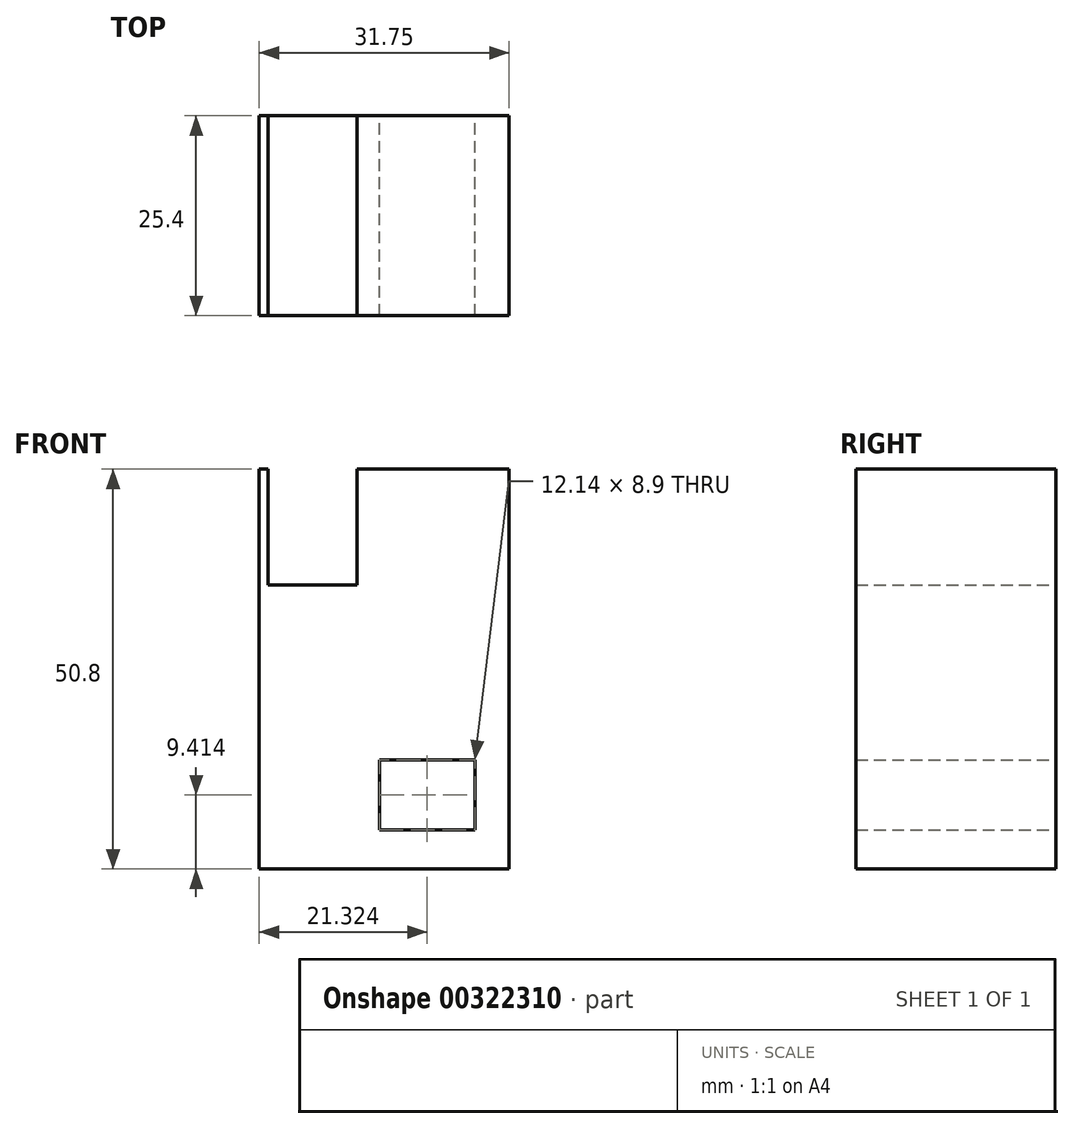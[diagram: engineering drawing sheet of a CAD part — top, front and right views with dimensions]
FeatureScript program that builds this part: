
annotation { "Feature Type Name" : "Feature", "Feature Type Description" : "" }
export const myFeature = defineFeature(function(context is Context, id is Id, definition is map)
    precondition{}
    {
        {
            var Q0;
            Q0=qCreatedBy(makeId("Front.planeOp"),FACE);
            var sketch = newSketch(context, id + "F0", { "sketchPlane" : qUnion([Q0])});
            skLineSegment(sketch, "E0.bottom", {"start": v(25.4, -25.4) * mm, "end": v(-25.4, -25.4) * mm});
            skLineSegment(sketch, "E0.top", {"start": v(25.4, 25.4) * mm, "end": v(-25.4, 25.4) * mm});
            skLineSegment(sketch, "E0.left", {"start": v(25.4, -25.4) * mm, "end": v(25.4, 25.4) * mm});
            skLineSegment(sketch, "E0.right", {"start": v(-25.4, -25.4) * mm, "end": v(-25.4, 25.4) * mm});
            skPoint(sketch, "E0.middle", {"position": v(0, 0) * mm});
            skLineSegment(sketch, "E1", {"start": v(-25.4, -25.4) * mm, "end": v(0, -69.4) * mm});
            skLineSegment(sketch, "E2", {"start": v(25.4, -25.4) * mm, "end": v(0, -69.4) * mm});
            skLineSegment(sketch, "E3", {"start": v(-5.26, 25.4) * mm, "end": v(-5.26, 10.72) * mm});
            skLineSegment(sketch, "E4", {"start": v(6.07, 25.4) * mm, "end": v(6.07, 10.72) * mm});
            skLineSegment(sketch, "E5", {"start": v(-5.26, 10.72) * mm, "end": v(6.07, 10.72) * mm});
            skLineSegment(sketch, "E6", {"start": v(-20.24, -11.53) * mm, "end": v(-10.52, -11.53) * mm});
            skLineSegment(sketch, "E7", {"start": v(-20.24, -11.53) * mm, "end": v(-20.24, -20.84) * mm});
            skLineSegment(sketch, "E8", {"start": v(-10.52, -11.53) * mm, "end": v(-10.52, -21.25) * mm});
            skLineSegment(sketch, "E9", {"start": v(-10.52, -21.25) * mm, "end": v(-20.24, -20.84) * mm});
            skLineSegment(sketch, "E10", {"start": v(8.9, -11.53) * mm, "end": v(21.04, -11.53) * mm});
            skLineSegment(sketch, "E11", {"start": v(8.9, -11.53) * mm, "end": v(8.9, -20.44) * mm});
            skLineSegment(sketch, "E12", {"start": v(8.9, -20.44) * mm, "end": v(21.04, -20.44) * mm});
            skLineSegment(sketch, "E13", {"start": v(21.04, -20.44) * mm, "end": v(21.04, -11.53) * mm});
            skLineSegment(sketch, "E14", {"start": v(-15.38, -11.53) * mm, "end": v(-15.38, -21.04) * mm});
            skLineSegment(sketch, "E15", {"start": v(-20.24, -16.19) * mm, "end": v(-10.52, -16.6) * mm});
            skLineSegment(sketch, "E16", {"start": v(14.97, -11.53) * mm, "end": v(14.97, -21.04) * mm});
            skLineSegment(sketch, "E17", {"start": v(21.04, -15.99) * mm, "end": v(8.9, -15.99) * mm});
            skLineSegment(sketch, "E18.0", {"start": v(-6.35, -25.4) * mm, "end": v(-6.35, 25.4) * mm});
            skSolve(sketch);
        }
        {
            var Q0;
            {var subQ5=sQuery(id+"F0.wireOp",EDGE,"E0.left");Q0=makeQuery(id+"F0.imprint","IMPRINT",FACE,{"disambiguationData":[TD([[makeQuery(id+"F0.imprint","IMPRINT",EDGE,{"derivedFrom":subQ5}),1.0]])]});}
            var sketch = newSketch(context, id + "F1", { "sketchPlane" : qUnion([Q0])});
            skSolve(sketch);
        }
        {
            var Q0;
            Q0 = qSketchRegion(id + "F1", true);
            var Q1;
            {var subQ5=sQuery(id+"F0.wireOp",EDGE,"E0.left");Q1=makeQuery(id+"F0.imprint","IMPRINT",FACE,{"disambiguationData":[TD([[makeQuery(id+"F0.imprint","IMPRINT",EDGE,{"derivedFrom":subQ5}),1.0]])]});}
            extrude(context, id + "F2", {"entities" : qUnion([Q0, Q1]), "depth" : 25.4 * mm});
        }
    });
